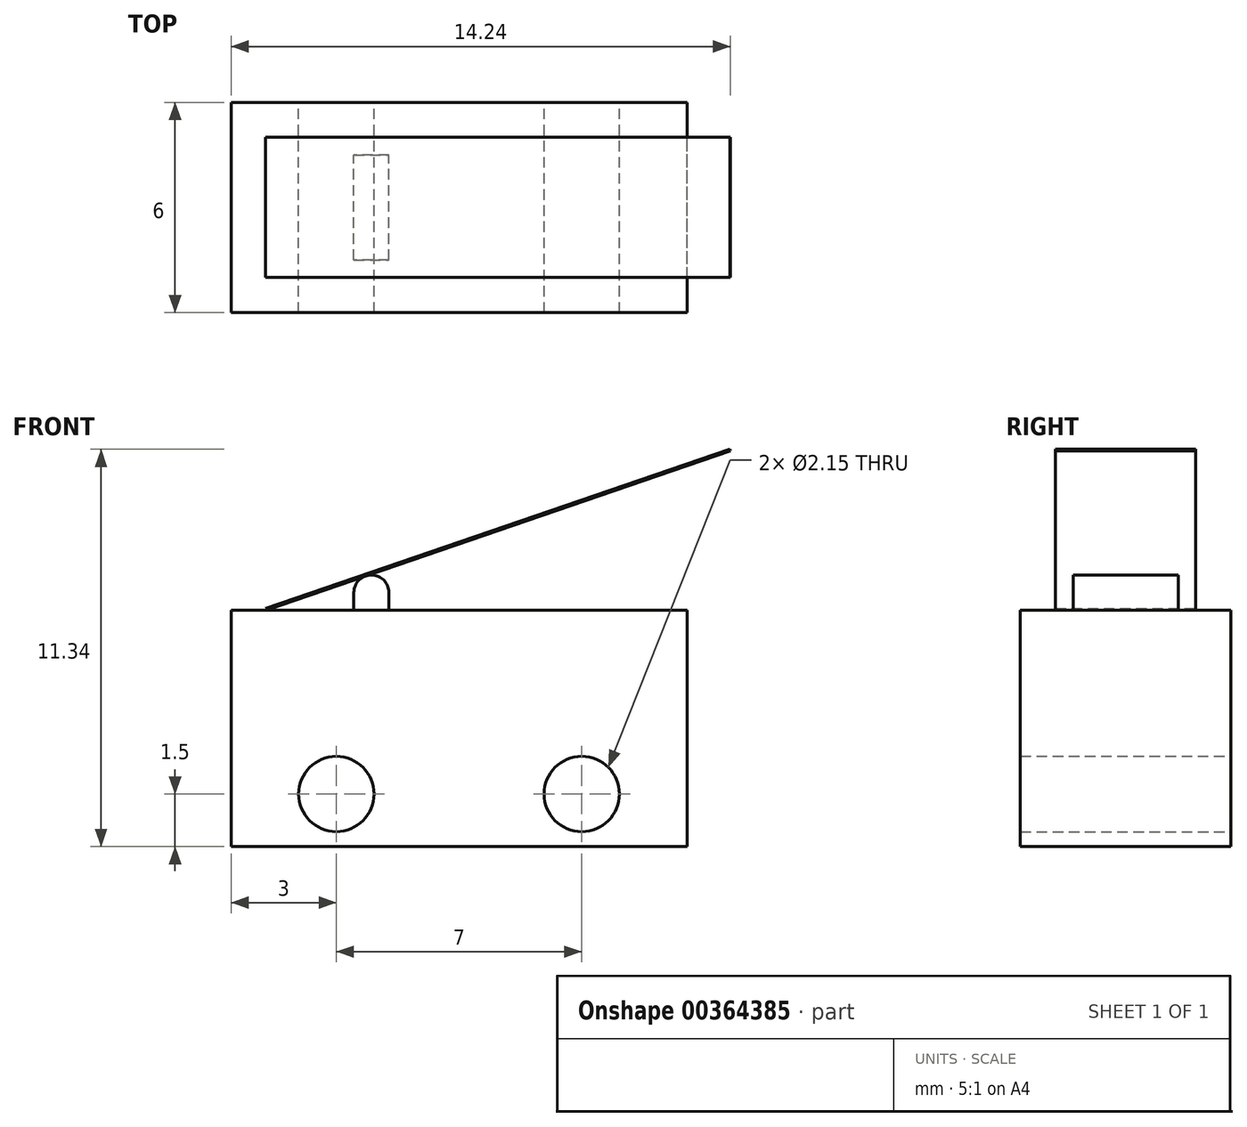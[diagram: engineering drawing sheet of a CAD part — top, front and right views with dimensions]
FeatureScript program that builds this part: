
annotation { "Feature Type Name" : "Feature", "Feature Type Description" : "" }
export const myFeature = defineFeature(function(context is Context, id is Id, definition is map)
    precondition{}
    {
        {
            var Q0;
            Q0=qCreatedBy(makeId("Front.planeOp"),FACE);
            var sketch = newSketch(context, id + "F0", { "sketchPlane" : qUnion([Q0])});
            skLineSegment(sketch, "E0.bottom", {"start": v(-13, 6.75) * mm, "end": v(0, 6.75) * mm});
            skLineSegment(sketch, "E0.top", {"start": v(-13, 0) * mm, "end": v(0, 0) * mm});
            skLineSegment(sketch, "E0.left", {"start": v(-13, 6.75) * mm, "end": v(-13, 0) * mm});
            skLineSegment(sketch, "E0.right", {"start": v(0, 6.75) * mm, "end": v(0, 0) * mm});
            skLineSegment(sketch, "E1", {"start": v(-10, 1.5) * mm, "end": v(-3, 1.5) * mm, "construction": true});
            skPoint(sketch, "E2", {"position": v(-6.5, 1.5) * mm});
            skPoint(sketch, "E3", {"position": v(-6.5, 6.75) * mm});
            skCircle(sketch, "E4", {"center": v(-10, 1.5) * mm, "radius": 1.07 * mm});
            skCircle(sketch, "E5", {"center": v(-3, 1.5) * mm, "radius": 1.07 * mm});
            skLineSegment(sketch, "E6", {"start": v(-9.5, 6.75) * mm, "end": v(-9.5, 7.25) * mm});
            skLineSegment(sketch, "E7", {"start": v(-8.5, 7.25) * mm, "end": v(-8.5, 6.75) * mm});
            skArc(sketch, "E8", {"start": v(-8.5, 7.25) * mm, "mid": v(-9, 7.75) * mm, "end": v(-9.5, 7.25) * mm});
            skLineSegment(sketch, "E9", {"start": v(-12, 6.75) * mm, "end": v(1.24, 11.3) * mm});
            skLineSegment(sketch, "E10", {"start": v(-12, 6.75) * mm, "end": v(-12.02, 6.8) * mm});
            skLineSegment(sketch, "E11", {"start": v(-12.02, 6.8) * mm, "end": v(1.23, 11.34) * mm});
            skLineSegment(sketch, "E12", {"start": v(1.23, 11.34) * mm, "end": v(1.24, 11.3) * mm});
            skSolve(sketch);
        }
        {
            var Q0;
            Q0=makeQuery(id+"F0.imprint","IMPRINT",FACE,{"disambiguationData":[TD([[makeQuery(id+"F0.imprint","IMPRINT",EDGE,{"derivedFrom":sQuery(id+"F0.wireOp",EDGE,"E0.top")}),1.0]])]});
            extrude(context, id + "F1", {"entities" : qUnion([Q0]), "depth" : 6 * mm, "offsetDistance" : 25 * mm, "symmetric" : true});
        }
        {
            var Q0;
            {var subQ3=sQuery(id+"F0.wireOp",EDGE,"E6");Q0=makeQuery(id+"F0.imprint","IMPRINT",FACE,{"disambiguationData":[TD([[makeQuery(id+"F0.imprint","IMPRINT",EDGE,{"derivedFrom":subQ3}),-1.0]])]});}
            extrude(context, id + "F2", {"entities" : qUnion([Q0]), "depth" : 3 * mm, "offsetDistance" : 25 * mm, "symmetric" : true});
        }
        {
            var Q0;
            {var subQ0=sQuery(id+"F0.wireOp",EDGE,"E10");Q0=makeQuery(id+"F0.imprint","IMPRINT",FACE,{"disambiguationData":[TD([[makeQuery(id+"F0.imprint","IMPRINT",EDGE,{"derivedFrom":subQ0}),-1.0]])]});}
            extrude(context, id + "F3", {"entities" : qUnion([Q0]), "operationType" : NewBodyOperationType.ADD, "depth" : 4 * mm, "offsetDistance" : 25 * mm, "symmetric" : true});
        }
    });
